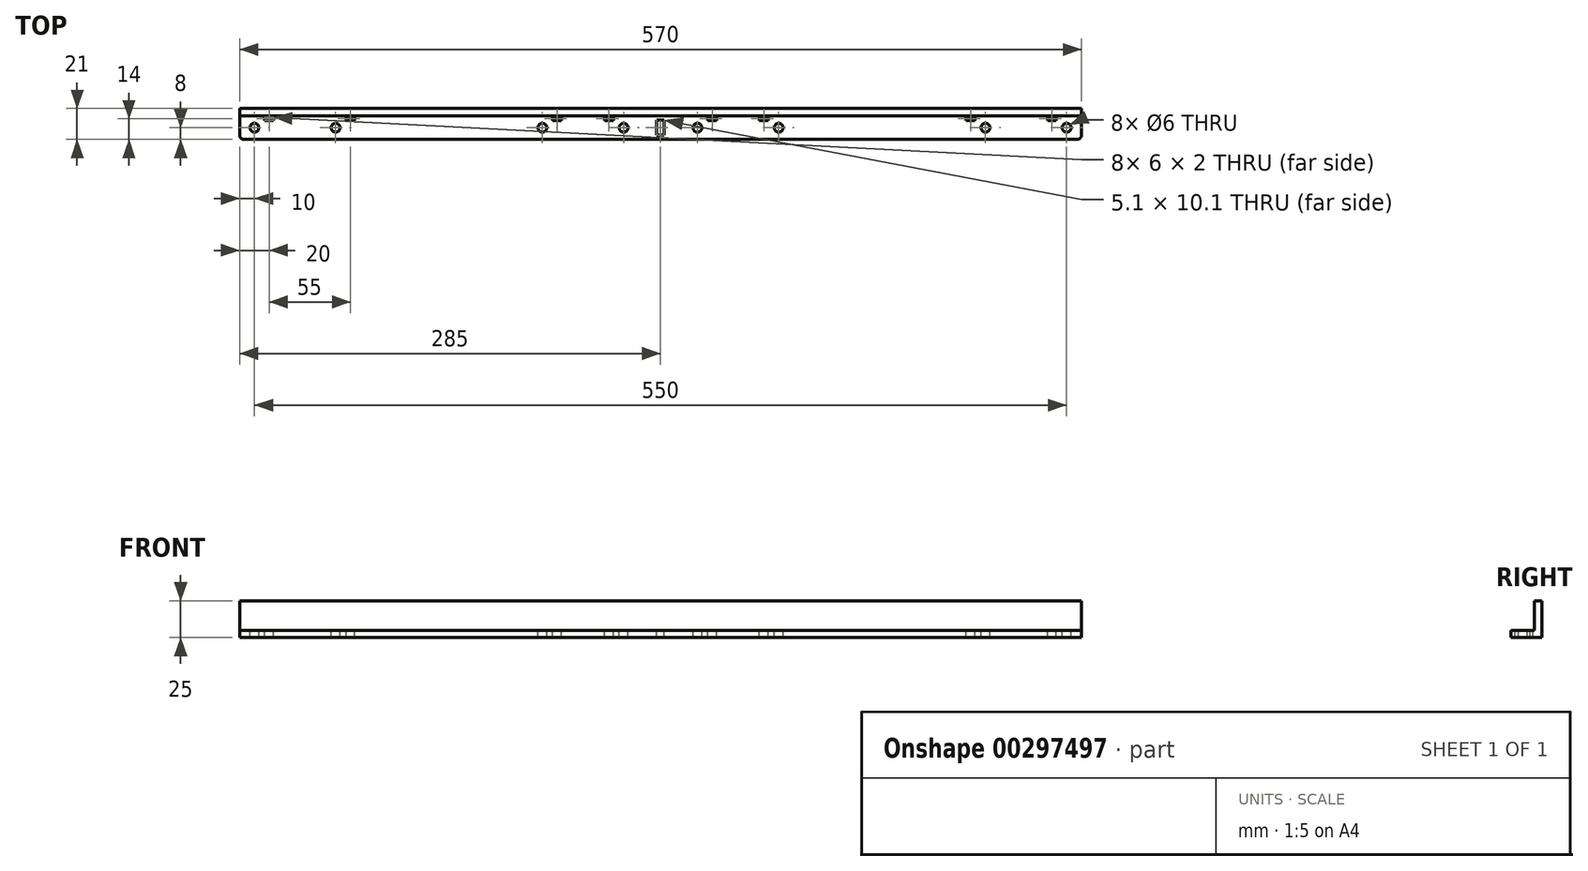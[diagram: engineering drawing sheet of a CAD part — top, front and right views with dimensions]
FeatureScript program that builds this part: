
annotation { "Feature Type Name" : "Feature", "Feature Type Description" : "" }
export const myFeature = defineFeature(function(context is Context, id is Id, definition is map)
    precondition{}
    {
        {
            var Q0;
            Q0=qCreatedBy(makeId("Top.planeOp"),FACE);
            var sketch = newSketch(context, id + "F0", { "sketchPlane" : qUnion([Q0])});
            skCircle(sketch, "E0", {"center": v(-220, 0) * mm, "radius": 3 * mm});
            skPoint(sketch, "E1", {"position": v(0, 0) * mm});
            skLineSegment(sketch, "E2.bottom", {"start": v(-282, -8) * mm, "end": v(282, -8) * mm});
            skPoint(sketch, "E3", {"position": v(-80, 0) * mm});
            skPoint(sketch, "E4", {"position": v(-25, 0) * mm});
            skPoint(sketch, "E5", {"position": v(-275, 0) * mm});
            skPoint(sketch, "E6", {"position": v(-150, 0) * mm});
            skCircle(sketch, "E7", {"center": v(-275, 0) * mm, "radius": 3 * mm});
            skLineSegment(sketch, "E8.bottom", {"start": v(-268, 7) * mm, "end": v(-262, 7) * mm});
            skLineSegment(sketch, "E8.top", {"start": v(-268, 5) * mm, "end": v(-262, 5) * mm});
            skLineSegment(sketch, "E8.left", {"start": v(-268, 7) * mm, "end": v(-268, 5) * mm});
            skLineSegment(sketch, "E8.right", {"start": v(-262, 7) * mm, "end": v(-262, 5) * mm});
            skCircle(sketch, "E9", {"center": v(-80, 0) * mm, "radius": 3 * mm});
            skCircle(sketch, "E10", {"center": v(-25, 0) * mm, "radius": 3 * mm});
            skLineSegment(sketch, "E11", {"start": v(-285, 13) * mm, "end": v(-285, -5) * mm});
            skPoint(sketch, "E12", {"position": v(80, 0) * mm});
            skPoint(sketch, "E13", {"position": v(220, 0) * mm});
            skPoint(sketch, "E14", {"position": v(275, 0) * mm});
            skPoint(sketch, "E15", {"position": v(25, 0) * mm});
            skPoint(sketch, "E16", {"position": v(150, 0) * mm});
            skCircle(sketch, "E17", {"center": v(25, 0) * mm, "radius": 3 * mm});
            skLineSegment(sketch, "E18.bottom", {"start": v(-213, 7) * mm, "end": v(-207, 7) * mm});
            skLineSegment(sketch, "E18.top", {"start": v(-213, 5) * mm, "end": v(-207, 5) * mm});
            skLineSegment(sketch, "E18.left", {"start": v(-213, 7) * mm, "end": v(-213, 5) * mm});
            skLineSegment(sketch, "E18.right", {"start": v(-207, 7) * mm, "end": v(-207, 5) * mm});
            skLineSegment(sketch, "E19.bottom", {"start": v(-73, 7) * mm, "end": v(-67, 7) * mm});
            skLineSegment(sketch, "E19.top", {"start": v(-73, 5) * mm, "end": v(-67, 5) * mm});
            skLineSegment(sketch, "E19.left", {"start": v(-73, 7) * mm, "end": v(-73, 5) * mm});
            skLineSegment(sketch, "E19.right", {"start": v(-67, 7) * mm, "end": v(-67, 5) * mm});
            skLineSegment(sketch, "E20.bottom", {"start": v(67, 7) * mm, "end": v(73, 7) * mm});
            skLineSegment(sketch, "E20.top", {"start": v(67, 5) * mm, "end": v(73, 5) * mm});
            skLineSegment(sketch, "E20.left", {"start": v(67, 7) * mm, "end": v(67, 5) * mm});
            skLineSegment(sketch, "E20.right", {"start": v(73, 7) * mm, "end": v(73, 5) * mm});
            skCircle(sketch, "E21", {"center": v(80, 0) * mm, "radius": 3 * mm});
            skLineSegment(sketch, "E22.bottom", {"start": v(207, 7) * mm, "end": v(213, 7) * mm});
            skLineSegment(sketch, "E22.top", {"start": v(207, 5) * mm, "end": v(213, 5) * mm});
            skLineSegment(sketch, "E22.left", {"start": v(207, 7) * mm, "end": v(207, 5) * mm});
            skLineSegment(sketch, "E22.right", {"start": v(213, 7) * mm, "end": v(213, 5) * mm});
            skCircle(sketch, "E23", {"center": v(220, 0) * mm, "radius": 3 * mm});
            skLineSegment(sketch, "E24.bottom", {"start": v(262, 7) * mm, "end": v(268, 7) * mm});
            skLineSegment(sketch, "E24.top", {"start": v(262, 5) * mm, "end": v(268, 5) * mm});
            skLineSegment(sketch, "E24.left", {"start": v(262, 7) * mm, "end": v(262, 5) * mm});
            skLineSegment(sketch, "E24.right", {"start": v(268, 7) * mm, "end": v(268, 5) * mm});
            skCircle(sketch, "E25", {"center": v(275, 0) * mm, "radius": 3 * mm});
            skLineSegment(sketch, "E26", {"start": v(285, 13) * mm, "end": v(285, -5) * mm});
            skLineSegment(sketch, "E27.bottom", {"start": v(32, 7) * mm, "end": v(38, 7) * mm});
            skLineSegment(sketch, "E27.top", {"start": v(32, 5) * mm, "end": v(38, 5) * mm});
            skLineSegment(sketch, "E27.left", {"start": v(32, 7) * mm, "end": v(32, 5) * mm});
            skLineSegment(sketch, "E27.right", {"start": v(38, 7) * mm, "end": v(38, 5) * mm});
            skLineSegment(sketch, "E28.bottom", {"start": v(-38, 7) * mm, "end": v(-32, 7) * mm});
            skLineSegment(sketch, "E28.top", {"start": v(-38, 5) * mm, "end": v(-32, 5) * mm});
            skLineSegment(sketch, "E28.left", {"start": v(-38, 7) * mm, "end": v(-38, 5) * mm});
            skLineSegment(sketch, "E28.right", {"start": v(-32, 7) * mm, "end": v(-32, 5) * mm});
            skLineSegment(sketch, "E29", {"start": v(-285, 13) * mm, "end": v(285, 13) * mm});
            skLineSegment(sketch, "E30.top", {"start": v(-285, 8) * mm, "end": v(285, 8) * mm});
            skLineSegment(sketch, "E30.left", {"start": v(-285, 13) * mm, "end": v(-285, 8) * mm});
            skLineSegment(sketch, "E30.right", {"start": v(285, 13) * mm, "end": v(285, 8) * mm});
            skLineSegment(sketch, "E31.bottom", {"start": v(2.55, -5.05) * mm, "end": v(-2.55, -5.05) * mm});
            skLineSegment(sketch, "E31.top", {"start": v(2.55, 5.05) * mm, "end": v(-2.55, 5.05) * mm});
            skLineSegment(sketch, "E31.left", {"start": v(2.55, -5.05) * mm, "end": v(2.55, 5.05) * mm});
            skLineSegment(sketch, "E31.right", {"start": v(-2.55, -5.05) * mm, "end": v(-2.55, 5.05) * mm});
            skPoint(sketch, "E32.visualSharp", {"position": v(-285, -8) * mm});
            skArc(sketch, "E32.filletArc", {"start": v(-285, -5) * mm, "mid": v(-284.12, -7.12) * mm, "end": v(-282, -8) * mm});
            skPoint(sketch, "E33.visualSharp", {"position": v(285, -8) * mm});
            skArc(sketch, "E33.filletArc", {"start": v(282, -8) * mm, "mid": v(284.12, -7.12) * mm, "end": v(285, -5) * mm});
            skSolve(sketch);
        }
        {
            var Q0;
            Q0=makeQuery(id+"F0.imprint","IMPRINT",FACE,{"disambiguationData":[TD([[makeQuery(id+"F0.imprint","IMPRINT",EDGE,{"derivedFrom":sQuery(id+"F0.wireOp",EDGE,"E29")}),-1.0]])]});
            extrude(context, id + "F1", {"entities" : qUnion([Q0]), "depth" : 20 * mm});
        }
        {
            var Q0;
            Q0 = qSketchRegion(id + "F0", true);
            extrude(context, id + "F2", {"entities" : qUnion([Q0]), "operationType" : NewBodyOperationType.ADD, "oppositeDirection" : true, "depth" : 5 * mm});
        }
    });
